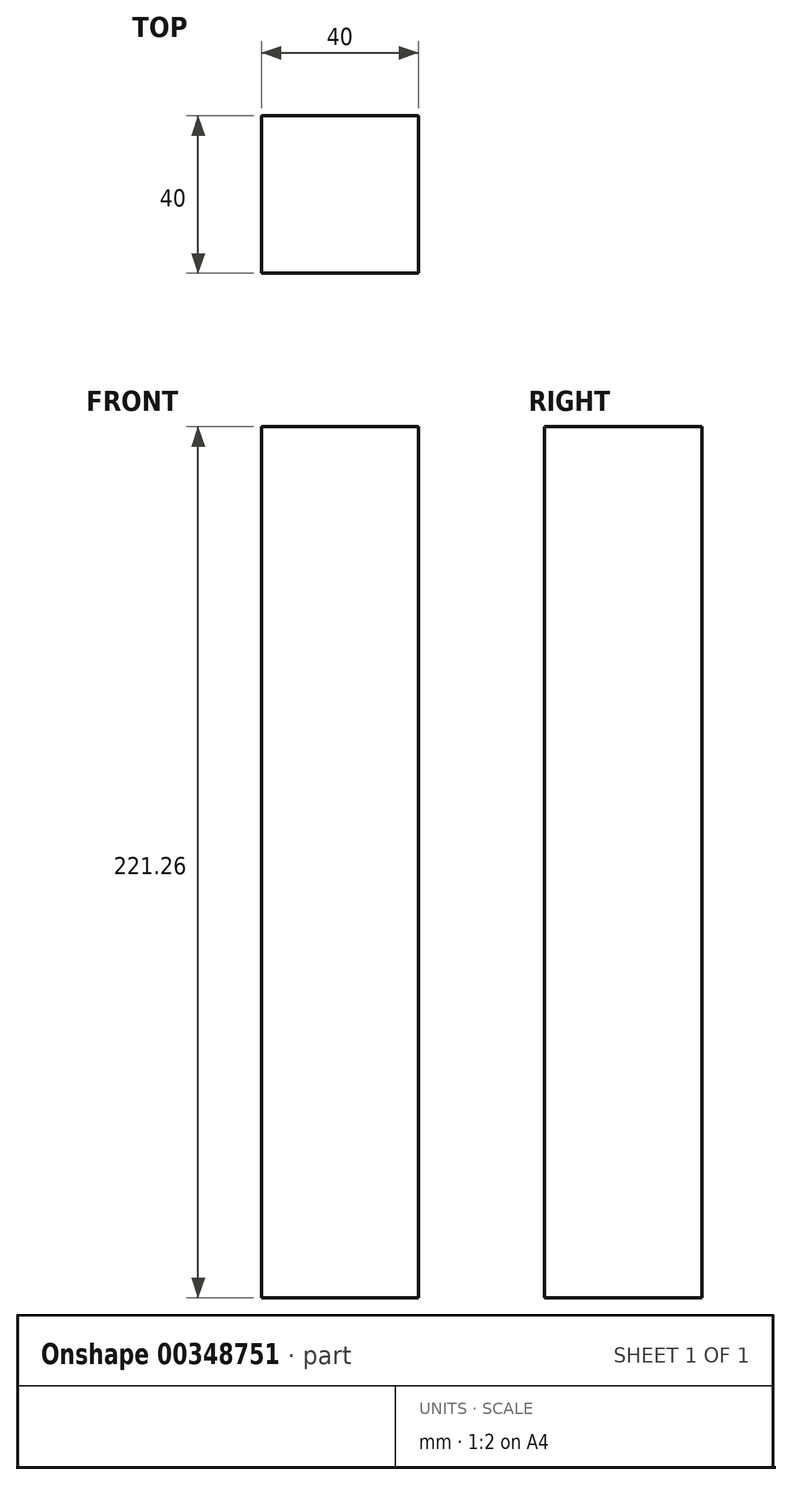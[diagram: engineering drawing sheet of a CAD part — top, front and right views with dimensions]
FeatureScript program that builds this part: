
annotation { "Feature Type Name" : "Feature", "Feature Type Description" : "" }
export const myFeature = defineFeature(function(context is Context, id is Id, definition is map)
    precondition{}
    {
        {
            var Q0;
            Q0=qCreatedBy(makeId("Right.planeOp"),FACE);
            var sketch = newSketch(context, id + "F0", { "sketchPlane" : qUnion([Q0])});
            skLineSegment(sketch, "E0.bottom", {"start": v(5.15, -32.79) * mm, "end": v(-34.85, -32.79) * mm});
            skLineSegment(sketch, "E0.top", {"start": v(5.15, 188.47) * mm, "end": v(-34.85, 188.47) * mm});
            skLineSegment(sketch, "E0.left", {"start": v(5.15, -32.79) * mm, "end": v(5.15, 188.47) * mm});
            skLineSegment(sketch, "E0.right", {"start": v(-34.85, -32.79) * mm, "end": v(-34.85, 188.47) * mm});
            skPoint(sketch, "E0.middle", {"position": v(-14.85, 77.84) * mm});
            skSolve(sketch);
        }
        {
            var Q0;
            Q0 = qSketchRegion(id + "F0", true);
            extrude(context, id + "F1", {"entities" : qUnion([Q0]), "depth" : 40 * mm});
        }
    });
